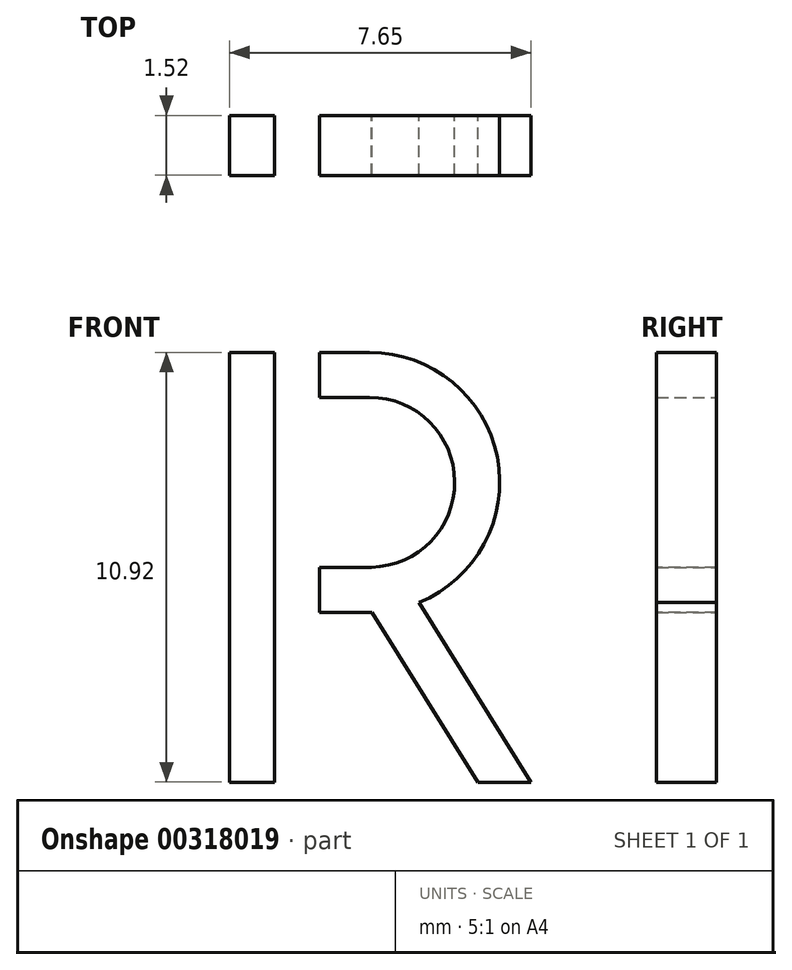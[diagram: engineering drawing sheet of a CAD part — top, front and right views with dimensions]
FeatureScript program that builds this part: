
annotation { "Feature Type Name" : "Feature", "Feature Type Description" : "" }
export const myFeature = defineFeature(function(context is Context, id is Id, definition is map)
    precondition{}
    {
        {
            var Q0;
            Q0=qCreatedBy(makeId("Front.planeOp"),FACE);
            var sketch = newSketch(context, id + "F0", { "sketchPlane" : qUnion([Q0])});
            skLineSegment(sketch, "E0", {"start": v(-24.03, -7.47) * mm, "end": v(-24.03, 3.45) * mm});
            skLineSegment(sketch, "E1", {"start": v(-24.03, 3.45) * mm, "end": v(-20.47, 3.45) * mm});
            skLineSegment(sketch, "E2", {"start": v(-22.88, -2.01) * mm, "end": v(-20.42, -2.01) * mm});
            skLineSegment(sketch, "E3.0", {"start": v(-22.88, -3.15) * mm, "end": v(-20.41, -3.15) * mm});
            skLineSegment(sketch, "E4", {"start": v(-24.03, -7.47) * mm, "end": v(-22.88, -7.47) * mm});
            skLineSegment(sketch, "E5.0", {"start": v(-22.88, 2.3) * mm, "end": v(-20.47, 2.3) * mm});
            skArc(sketch, "E6", {"start": v(-20.42, -2.01) * mm, "mid": v(-18.31, 0.17) * mm, "end": v(-20.47, 2.3) * mm});
            skLineSegment(sketch, "E7", {"start": v(-22.88, -7.47) * mm, "end": v(-22.88, -3.15) * mm});
            skLineSegment(sketch, "E8", {"start": v(-22.88, -2.01) * mm, "end": v(-22.88, 2.3) * mm});
            skLineSegment(sketch, "E9", {"start": v(-20.41, -3.15) * mm, "end": v(-17.73, -7.47) * mm});
            skLineSegment(sketch, "E10", {"start": v(-17.73, -7.47) * mm, "end": v(-16.38, -7.47) * mm});
            skLineSegment(sketch, "E11", {"start": v(-16.38, -7.47) * mm, "end": v(-19.22, -2.9) * mm});
            skArc(sketch, "E12.trimOffspring", {"start": v(-19.22, -2.9) * mm, "mid": v(-17.23, 0.79) * mm, "end": v(-20.47, 3.45) * mm});
            skPoint(sketch, "E13", {"position": v(3.84, -17.62) * mm});
            skPoint(sketch, "E14.orphan", {"position": v(-24.03, -2.01) * mm});
            skSolve(sketch);
        }
        {
            var Q0;
            Q0 = qSketchRegion(id + "F0", true);
            extrude(context, id + "F1", {"entities" : qUnion([Q0]), "depth" : 1.52 * mm});
        }
        {
            var Q0;
            Q0=makeQuery(id+"F1.opExtrude","CAP_FACE",FACE,{"disambiguationData":[OSD([sQuery(id+"F0.wireOp",EDGE,"E0"),sQuery(id+"F0.wireOp",EDGE,"E1"),sQuery(id+"F0.wireOp",EDGE,"E2"),sQuery(id+"F0.wireOp",EDGE,"E3.0"),sQuery(id+"F0.wireOp",EDGE,"E4"),sQuery(id+"F0.wireOp",EDGE,"E5.0"),sQuery(id+"F0.wireOp",EDGE,"E6"),sQuery(id+"F0.wireOp",EDGE,"E7"),sQuery(id+"F0.wireOp",EDGE,"E8"),sQuery(id+"F0.wireOp",EDGE,"E9"),sQuery(id+"F0.wireOp",EDGE,"E10"),sQuery(id+"F0.wireOp",EDGE,"E11"),sQuery(id+"F0.wireOp",EDGE,"E12.trimOffspring")])],"isStart":false});
            var sketch = newSketch(context, id + "F2", { "sketchPlane" : qUnion([Q0])});
            skPoint(sketch, "E15.0", {"position": v(3.84, -17.62) * mm});
            skLineSegment(sketch, "E16.bottom", {"start": v(-22.88, 3.45) * mm, "end": v(-21.74, 3.45) * mm});
            skLineSegment(sketch, "E16.top", {"start": v(-22.88, -3.15) * mm, "end": v(-21.74, -3.15) * mm});
            skLineSegment(sketch, "E16.left", {"start": v(-22.88, 3.45) * mm, "end": v(-22.88, -3.15) * mm});
            skLineSegment(sketch, "E16.right", {"start": v(-21.74, 3.45) * mm, "end": v(-21.74, -3.15) * mm});
            skSolve(sketch);
        }
        {
            var Q0;
            Q0 = qSketchRegion(id + "F2", true);
            extrude(context, id + "F3", {"entities" : qUnion([Q0]), "operationType" : NewBodyOperationType.REMOVE, "oppositeDirection" : true, "depth" : 25.4 * mm});
        }
    });
